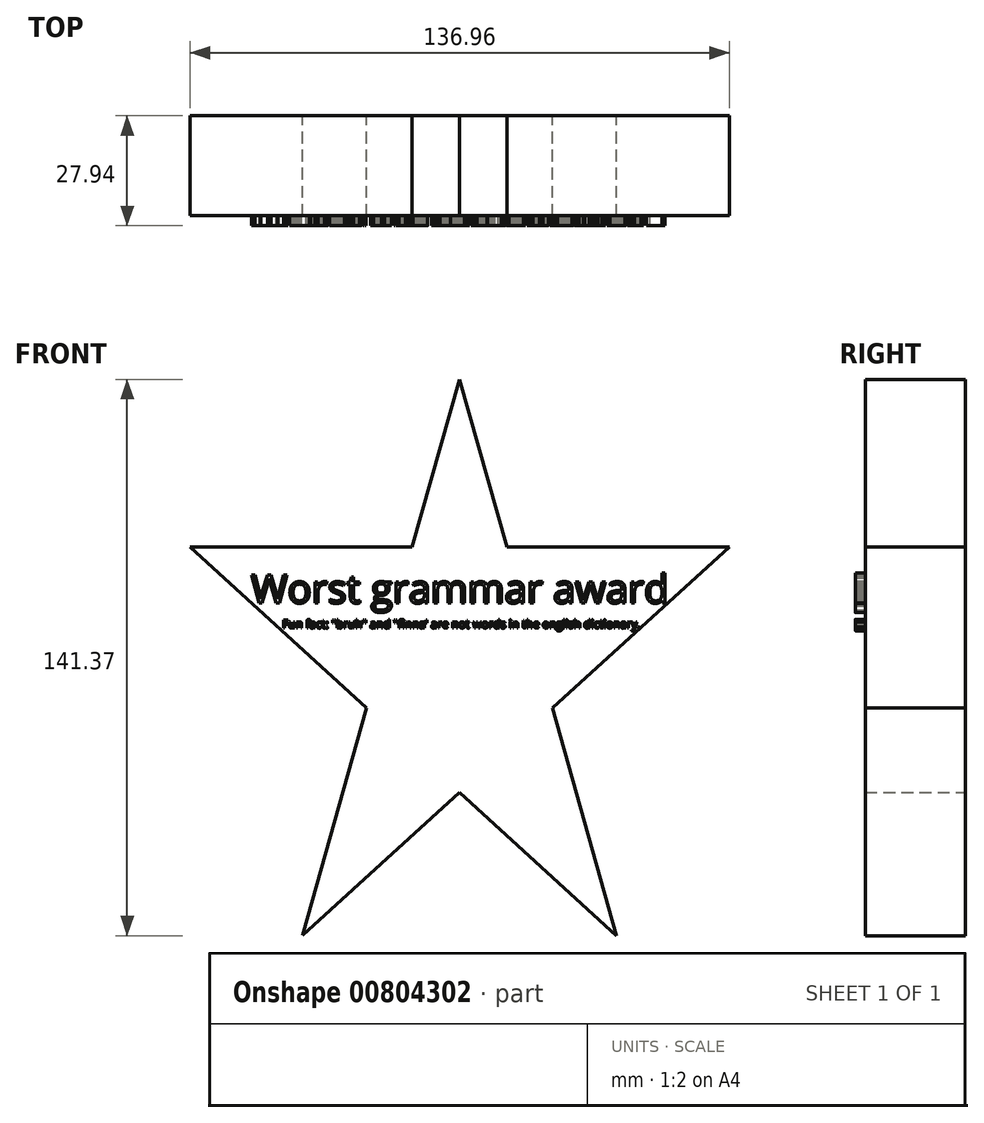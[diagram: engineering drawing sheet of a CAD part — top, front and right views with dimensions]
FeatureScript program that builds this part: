
annotation { "Feature Type Name" : "Feature", "Feature Type Description" : "" }
export const myFeature = defineFeature(function(context is Context, id is Id, definition is map)
    precondition{}
    {
        {
            var Q0;
            Q0=qCreatedBy(makeId("Front.planeOp"),FACE);
            var sketch = newSketch(context, id + "F0", { "sketchPlane" : qUnion([Q0])});
            skCircle(sketch, "E0", {"center": v(0, 0) * mm, "radius": 76.3 * mm});
            skLineSegment(sketch, "E1", {"start": v(39.84, -65.07) * mm, "end": v(-68.48, 33.65) * mm});
            skLineSegment(sketch, "E2", {"start": v(-68.48, 33.65) * mm, "end": v(68.48, 33.65) * mm});
            skLineSegment(sketch, "E3", {"start": v(68.48, 33.65) * mm, "end": v(-40, -64.98) * mm});
            skLineSegment(sketch, "E4", {"start": v(-40, -64.98) * mm, "end": v(0, 76.3) * mm});
            skLineSegment(sketch, "E5", {"start": v(0, 76.3) * mm, "end": v(39.84, -65.07) * mm});
            skSolve(sketch);
        }
        {
            var Q0;
            Q0=sQuery(id+"F0.wireOp",EDGE,"E0");
            extrude(context, id + "F1", {"bodyType" : ToolBodyType.SURFACE, "surfaceEntities" : qUnion([Q0]), "depth" : 25.4 * mm, "offsetDistance" : 25.4 * mm});
        }
        {
            var Q0;
            {var subQ1=sQuery(id+"F0.wireOp",EDGE,"E1");var subQ3=sQuery(id+"F0.wireOp",EDGE,"E3");var subQ4=makeQuery(id+"F0.imprint","INTERSECT",VERTEX,{"derivedFrom":[subQ1,subQ3]});Q0=makeQuery(id+"F0.imprint","IMPRINT",FACE,{"disambiguationData":[TD([[makeQuery(id+"F0.imprint","IMPRINT",EDGE,{"disambiguationData":[TD([[subQ4,1.0]])],"derivedFrom":subQ3}),1.0]])]});}
            var Q1;
            {var subQ0=sQuery(id+"F0.wireOp",EDGE,"E3");var subQ1=sQuery(id+"F0.wireOp",EDGE,"E1");var subQ2=makeQuery(id+"F0.imprint","INTERSECT",VERTEX,{"derivedFrom":[subQ1,subQ0]});Q1=makeQuery(id+"F0.imprint","IMPRINT",FACE,{"disambiguationData":[TD([[makeQuery(id+"F0.imprint","IMPRINT",EDGE,{"disambiguationData":[TD([[subQ2,-1.0]])],"derivedFrom":subQ1}),1.0]])]});}
            var Q2;
            {var subQ1=sQuery(id+"F0.wireOp",EDGE,"E1");var subQ3=sQuery(id+"F0.wireOp",EDGE,"E4");var subQ4=makeQuery(id+"F0.imprint","INTERSECT",VERTEX,{"derivedFrom":[subQ1,subQ3]});Q2=makeQuery(id+"F0.imprint","IMPRINT",FACE,{"disambiguationData":[TD([[makeQuery(id+"F0.imprint","IMPRINT",EDGE,{"disambiguationData":[TD([[subQ4,-1.0]])],"derivedFrom":subQ3}),1.0]])]});}
            var Q3;
            {var subQ1=sQuery(id+"F0.wireOp",EDGE,"E1");var subQ5=sQuery(id+"F0.wireOp",EDGE,"E3");var subQ6=makeQuery(id+"F0.imprint","INTERSECT",VERTEX,{"derivedFrom":[subQ1,subQ5]});Q3=makeQuery(id+"F0.imprint","IMPRINT",FACE,{"disambiguationData":[TD([[makeQuery(id+"F0.imprint","IMPRINT",EDGE,{"disambiguationData":[TD([[subQ6,-1.0]])],"derivedFrom":subQ1}),-1.0]])]});}
            var Q4;
            {var subQ0=sQuery(id+"F0.wireOp",EDGE,"E4");var subQ1=sQuery(id+"F0.wireOp",EDGE,"E2");var subQ2=makeQuery(id+"F0.imprint","INTERSECT",VERTEX,{"derivedFrom":[subQ1,subQ0]});Q4=makeQuery(id+"F0.imprint","IMPRINT",FACE,{"disambiguationData":[TD([[makeQuery(id+"F0.imprint","IMPRINT",EDGE,{"disambiguationData":[TD([[subQ2,-1.0]])],"derivedFrom":subQ1}),1.0]])]});}
            var Q5;
            {var subQ1=sQuery(id+"F0.wireOp",EDGE,"E2");var subQ3=sQuery(id+"F0.wireOp",EDGE,"E5");var subQ4=makeQuery(id+"F0.imprint","INTERSECT",VERTEX,{"derivedFrom":[subQ1,subQ3]});Q5=makeQuery(id+"F0.imprint","IMPRINT",FACE,{"disambiguationData":[TD([[makeQuery(id+"F0.imprint","IMPRINT",EDGE,{"disambiguationData":[TD([[subQ4,-1.0]])],"derivedFrom":subQ3}),1.0]])]});}
            extrude(context, id + "F2", {"entities" : qUnion([Q0, Q1, Q2, Q3, Q4, Q5]), "depth" : 25.4 * mm, "offsetDistance" : 25.4 * mm});
        }
        {
            var Q0;
            Q0=makeQuery(id+"F2.opExtrude","CAP_FACE",FACE,{"disambiguationData":[OSD([sQuery(id+"F0.wireOp",EDGE,"E1"),sQuery(id+"F0.wireOp",EDGE,"E2"),sQuery(id+"F0.wireOp",EDGE,"E3"),sQuery(id+"F0.wireOp",EDGE,"E4"),sQuery(id+"F0.wireOp",EDGE,"E5")])],"isStart":false});
            var sketch = newSketch(context, id + "F3", { "sketchPlane" : qUnion([Q0])});
            skText(sketch, "E6", { "text": "Worst grammar award\n", "fontName": "OpenSans-Regular.ttf"});
            skText(sketch, "E7", { "text": "Fun fact: \"bruh\" and \"finna\' are not words in the english dictionary.", "fontName": "OpenSans-Regular.ttf"});
            const initialGuessF3  = {"E6": [-0.05306, 0.01944, 1, 0, 0.00725], "E7": [-0.04502, 0.01308, 1, 0, 0.00211]};
            skSetInitialGuess(sketch, initialGuessF3);
            skSolve(sketch);
        }
        {
            var Q0;
            Q0 = qSketchRegion(id + "F3", true);
            extrude(context, id + "F4", {"entities" : qUnion([Q0]), "operationType" : NewBodyOperationType.ADD, "depth" : 2.54 * mm, "offsetDistance" : 25.4 * mm});
        }
    });
